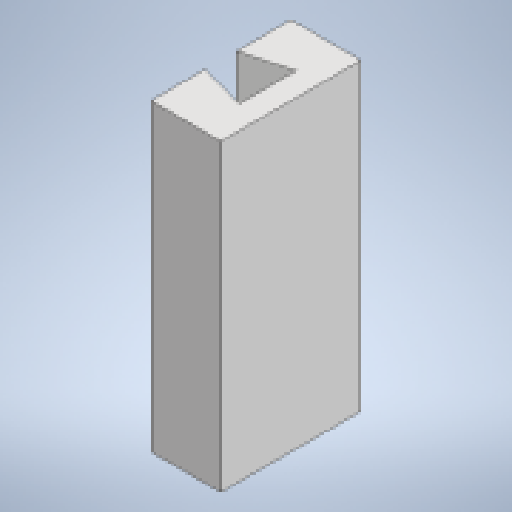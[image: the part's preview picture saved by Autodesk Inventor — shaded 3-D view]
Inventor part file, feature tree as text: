
AUTODESK INVENTOR PART (.ipt)
format: ipt  version: 2023 (Build 270158000, 158)  size: 144,896 bytes
history: native  units: mm
features: extrude x2, sketch x2, projected_geometry x1
ambient origin geometry x8: Origin, YZ Plane, XZ Plane, XY Plane, X Axis, Y Axis, Z Axis, Center Point
bodies: Solid1 (feature_tree)
feature tree (5):
  extrude  "Extrusion1"  Depth=30.0mm
  extrude  "Extrusion2"  Depth=10.0mm
  sketch  "Sketch1"  dims[d0=12.2mm d1=30.0mm]
  sketch  "Sketch2"  dims[d2=15.0mm d3=10.0mm d4=30.0deg d5=60.0mm d6=0.0mm d7=5.0mm d8=0.0mm d9=6.0mm]
  projected_geometry  "Projected Loop1"
